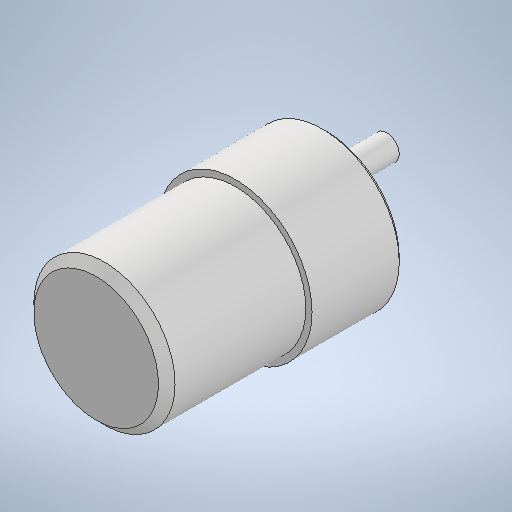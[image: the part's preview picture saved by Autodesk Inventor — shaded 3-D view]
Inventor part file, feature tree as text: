
AUTODESK INVENTOR PART (.ipt)
format: ipt  version: 2025.1 (Build 291241000, 241)  size: 259,072 bytes
history: native  units: mm
features: extrude x5, sketch x5, chamfer x3
ambient origin geometry x8: Origin, YZ Plane, XZ Plane, XY Plane, X Axis, Y Axis, Z Axis, Center Point
bodies: 实体1 (feature_tree)
feature tree (13):
  extrude  "拉伸1"  Depth=22.0mm TaperAngle=0.0deg
  extrude  "拉伸2"  Depth=33.5mm TaperAngle=0.0deg
  chamfer  "倒角1"  Distance=2.0mm Angle=45.0deg
  extrude  "拉伸3"  Depth=7.0mm
  extrude  "拉伸4"  Depth=6.0mm
  chamfer  "倒角2"  Distance=15.5mm
  extrude  "拉伸5"  Depth=1.0mm
  chamfer  "倒角3"  Distance=1.0mm
  sketch  "草图1"  dims[d0=37.0mm d1=22.0mm d2=0.0mm]
  sketch  "草图2"  dims[d3=34.0mm d4=33.5mm d5=0.0mm d6=2.0mm d7=2.0mm d8=45.0deg]
  sketch  "草图3"  dims[d9=10.0mm d10=7.0mm]
  sketch  "草图4"  dims[d11=6.0mm d12=0.0mm d13=6.0mm d14=15.5mm d15=0.0mm]
  sketch  "草图5"  dims[d16=0.5mm d17=2.0mm d18=45.0deg d19=22.0mm d20=1.0mm d21=0.0mm d22=1.0mm d23=2.0mm d24=45.0deg]
